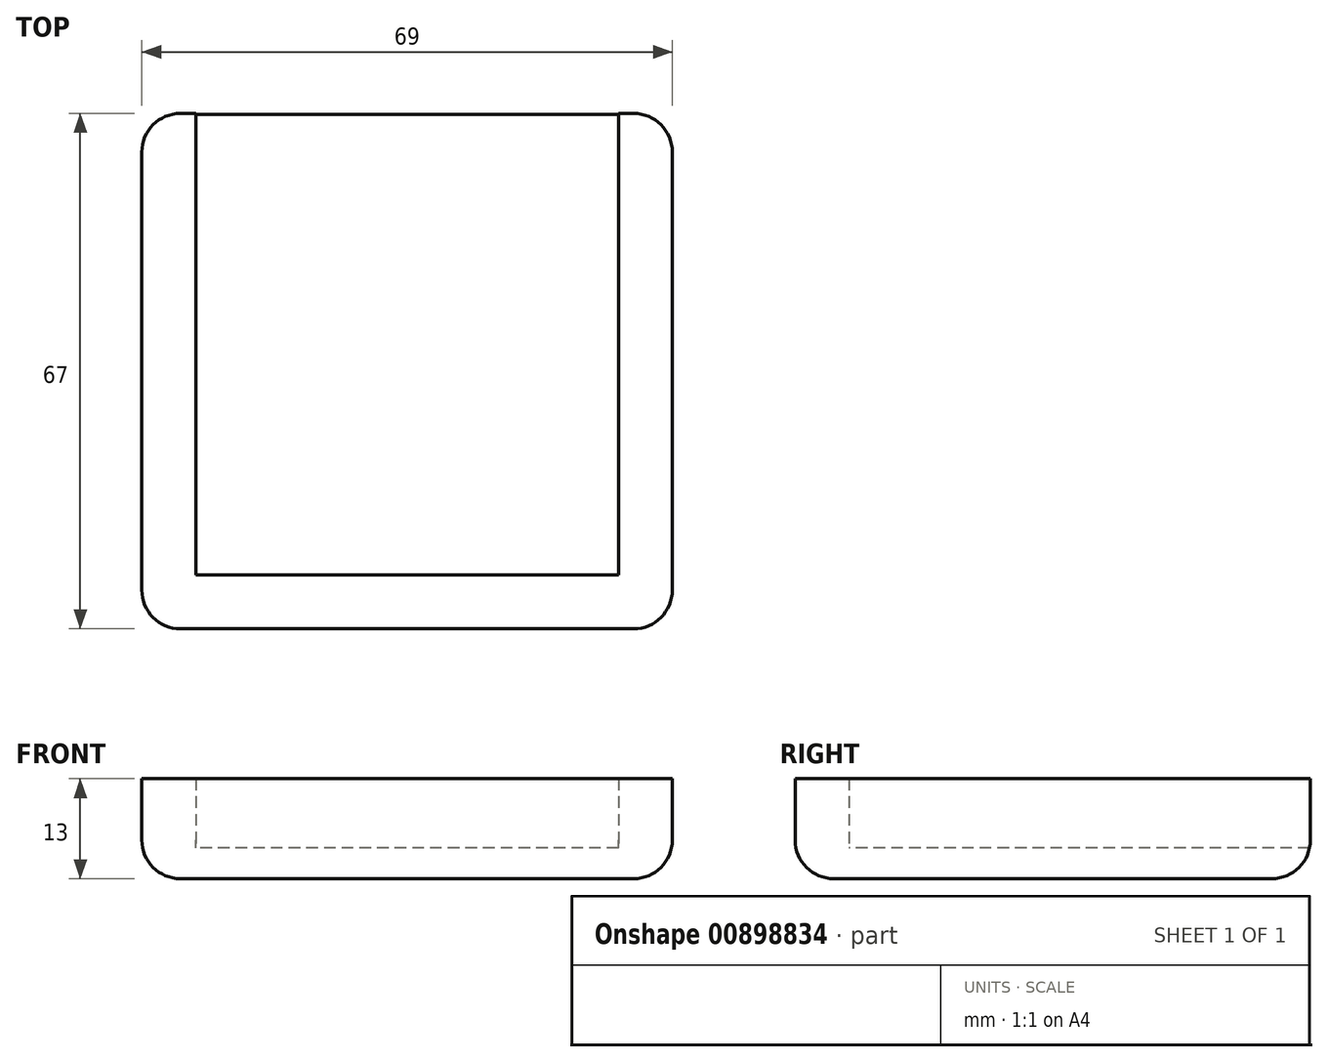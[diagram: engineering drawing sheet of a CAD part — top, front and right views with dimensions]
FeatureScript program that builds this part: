
annotation { "Feature Type Name" : "Feature", "Feature Type Description" : "" }
export const myFeature = defineFeature(function(context is Context, id is Id, definition is map)
    precondition{}
    {
        {
            var Q0;
            Q0=qCreatedBy(makeId("Top.planeOp"),FACE);
            var sketch = newSketch(context, id + "F0", { "sketchPlane" : qUnion([Q0])});
            skLineSegment(sketch, "E0.top", {"start": v(27.5, -30) * mm, "end": v(-27.5, -30) * mm});
            skLineSegment(sketch, "E0.left", {"start": v(27.5, 30) * mm, "end": v(27.5, -30) * mm});
            skLineSegment(sketch, "E0.right", {"start": v(-27.5, 30) * mm, "end": v(-27.5, -30) * mm});
            skPoint(sketch, "E0.middle", {"position": v(0, 0) * mm});
            skLineSegment(sketch, "E1", {"start": v(34.5, 30) * mm, "end": v(34.5, -37) * mm});
            skLineSegment(sketch, "E2", {"start": v(34.5, -37) * mm, "end": v(-34.5, -37) * mm});
            skLineSegment(sketch, "E3", {"start": v(-34.5, -37) * mm, "end": v(-34.5, 30) * mm});
            skLineSegment(sketch, "E4", {"start": v(-34.5, 30) * mm, "end": v(-27.5, 30) * mm});
            skLineSegment(sketch, "E5", {"start": v(-27.5, 30) * mm, "end": v(27.5, 30) * mm});
            skLineSegment(sketch, "E6", {"start": v(34.5, 30) * mm, "end": v(27.5, 30) * mm});
            skSolve(sketch);
        }
        {
            var Q0;
            Q0=makeQuery(id+"F0.imprint","IMPRINT",FACE,{"disambiguationData":[TD([[makeQuery(id+"F0.imprint","IMPRINT",EDGE,{"derivedFrom":sQuery(id+"F0.wireOp",EDGE,"E0.top")}),1.0]])]});
            extrude(context, id + "F1", {"entities" : qUnion([Q0]), "depth" : 9 * mm, "offsetDistance" : 25 * mm});
        }
        {
            var Q0;
            Q0=makeQuery(id+"F0.imprint","IMPRINT",FACE,{"disambiguationData":[TD([[makeQuery(id+"F0.imprint","IMPRINT",EDGE,{"derivedFrom":sQuery(id+"F0.wireOp",EDGE,"E0.top")}),1.0]])]});
            var Q1;
            Q1=makeQuery(id+"F0.imprint","IMPRINT",FACE,{"disambiguationData":[TD([[makeQuery(id+"F0.imprint","IMPRINT",EDGE,{"derivedFrom":sQuery(id+"F0.wireOp",EDGE,"E0.top")}),-1.0]])]});
            extrude(context, id + "F2", {"entities" : qUnion([Q0, Q1]), "operationType" : NewBodyOperationType.ADD, "oppositeDirection" : true, "depth" : 4 * mm, "offsetDistance" : 25 * mm});
        }
        {
            var Q0;
            Q0=makeQuery(id+"F2.opExtrude","CAP_EDGE",EDGE,{"disambiguationData":[OSD([sQuery(id+"F0.wireOp",EDGE,"E5"),sQuery(id+"F0.wireOp",EDGE,"E6")])],"isStart":false});
            var Q1;
            Q1=makeQuery(id+"F2.opExtrude","CAP_EDGE",EDGE,{"disambiguationData":[OSD([sQuery(id+"F0.wireOp",EDGE,"E4")])],"isStart":false});
            var Q2;
            Q2=makeQuery(id+"F2.opExtrude","CAP_EDGE",EDGE,{"disambiguationData":[OSD([sQuery(id+"F0.wireOp",EDGE,"E1")])],"isStart":false});
            var Q3;
            Q3=makeQuery(id+"F2.opExtrude","CAP_EDGE",EDGE,{"disambiguationData":[OSD([sQuery(id+"F0.wireOp",EDGE,"E3")])],"isStart":false});
            var Q4;
            Q4=makeQuery(id+"F2.opExtrude","CAP_EDGE",EDGE,{"disambiguationData":[OSD([sQuery(id+"F0.wireOp",EDGE,"E2")])],"isStart":false});
            fillet(context, id + "F3", {"entities" : qUnion([Q0, Q1, Q2, Q3, Q4]), "radius" : 5 * mm, "tangentPropagation" : true, "allowEdgeOverflow" : false});
        }
        {
            var Q0;
            {var subQ0=sQuery(id+"F0.wireOp",EDGE,"E3");var subQ1=sQuery(id+"F0.wireOp",EDGE,"E2");Q0=makeQuery(id+"F2.boolean.opBoolean","MERGE",EDGE,{"derivedFrom":[makeQuery(id+"F1.opExtrude","SWEPT_EDGE",EDGE,{"disambiguationData":[OSD([subQ1,subQ0])]}),makeQuery(id+"F2.opExtrude","SWEPT_EDGE",EDGE,{"disambiguationData":[OSD([subQ1,subQ0])]})]});}
            var Q1;
            {var subQ0=sQuery(id+"F0.wireOp",EDGE,"E2");var subQ1=sQuery(id+"F0.wireOp",EDGE,"E1");Q1=makeQuery(id+"F2.boolean.opBoolean","MERGE",EDGE,{"derivedFrom":[makeQuery(id+"F1.opExtrude","SWEPT_EDGE",EDGE,{"disambiguationData":[OSD([subQ1,subQ0])]}),makeQuery(id+"F2.opExtrude","SWEPT_EDGE",EDGE,{"disambiguationData":[OSD([subQ1,subQ0])]})]});}
            var Q2;
            {var subQ0=sQuery(id+"F0.wireOp",EDGE,"E6");var subQ1=sQuery(id+"F0.wireOp",EDGE,"E1");Q2=makeQuery(id+"F2.boolean.opBoolean","MERGE",EDGE,{"derivedFrom":[makeQuery(id+"F1.opExtrude","SWEPT_EDGE",EDGE,{"disambiguationData":[OSD([subQ1,subQ0])]}),makeQuery(id+"F2.opExtrude","SWEPT_EDGE",EDGE,{"disambiguationData":[OSD([subQ1,subQ0])]})]});}
            var Q3;
            {var subQ0=sQuery(id+"F0.wireOp",EDGE,"E4");var subQ1=sQuery(id+"F0.wireOp",EDGE,"E3");Q3=makeQuery(id+"F2.boolean.opBoolean","MERGE",EDGE,{"derivedFrom":[makeQuery(id+"F1.opExtrude","SWEPT_EDGE",EDGE,{"disambiguationData":[OSD([subQ1,subQ0])]}),makeQuery(id+"F2.opExtrude","SWEPT_EDGE",EDGE,{"disambiguationData":[OSD([subQ1,subQ0])]})]});}
            fillet(context, id + "F4", {"entities" : qUnion([Q0, Q1, Q2, Q3]), "radius" : 5 * mm, "tangentPropagation" : true, "allowEdgeOverflow" : false});
        }
    });
